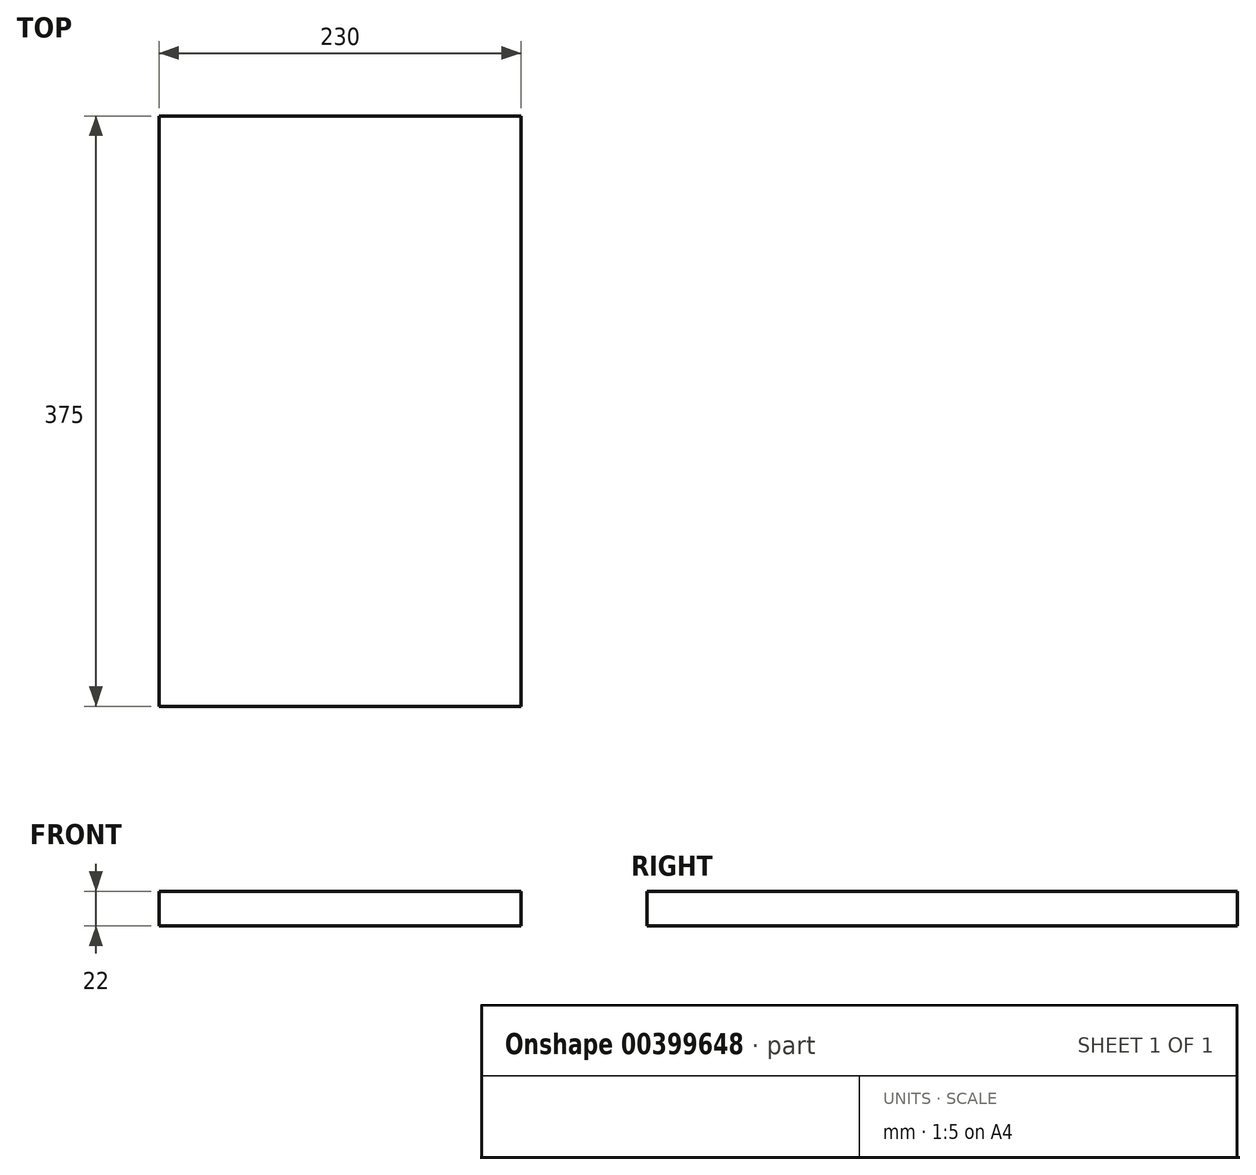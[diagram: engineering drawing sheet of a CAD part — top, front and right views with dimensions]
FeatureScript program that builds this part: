
annotation { "Feature Type Name" : "Feature", "Feature Type Description" : "" }
export const myFeature = defineFeature(function(context is Context, id is Id, definition is map)
    precondition{}
    {
        {
            var Q0;
            Q0=qCreatedBy(makeId("Top.planeOp"),FACE);
            var sketch = newSketch(context, id + "F0", { "sketchPlane" : qUnion([Q0])});
            skLineSegment(sketch, "E0.bottom", {"start": v(-115, 187.5) * mm, "end": v(115, 187.5) * mm});
            skLineSegment(sketch, "E0.top", {"start": v(-115, -187.5) * mm, "end": v(115, -187.5) * mm});
            skLineSegment(sketch, "E0.left", {"start": v(-115, 187.5) * mm, "end": v(-115, -187.5) * mm});
            skLineSegment(sketch, "E0.right", {"start": v(115, 187.5) * mm, "end": v(115, -187.5) * mm});
            skPoint(sketch, "E0.middle", {"position": v(0, 0) * mm});
            skSolve(sketch);
        }
        {
            var Q0;
            Q0 = qSketchRegion(id + "F0", true);
            extrude(context, id + "F1", {"entities" : qUnion([Q0]), "depth" : 22 * mm});
        }
    });
